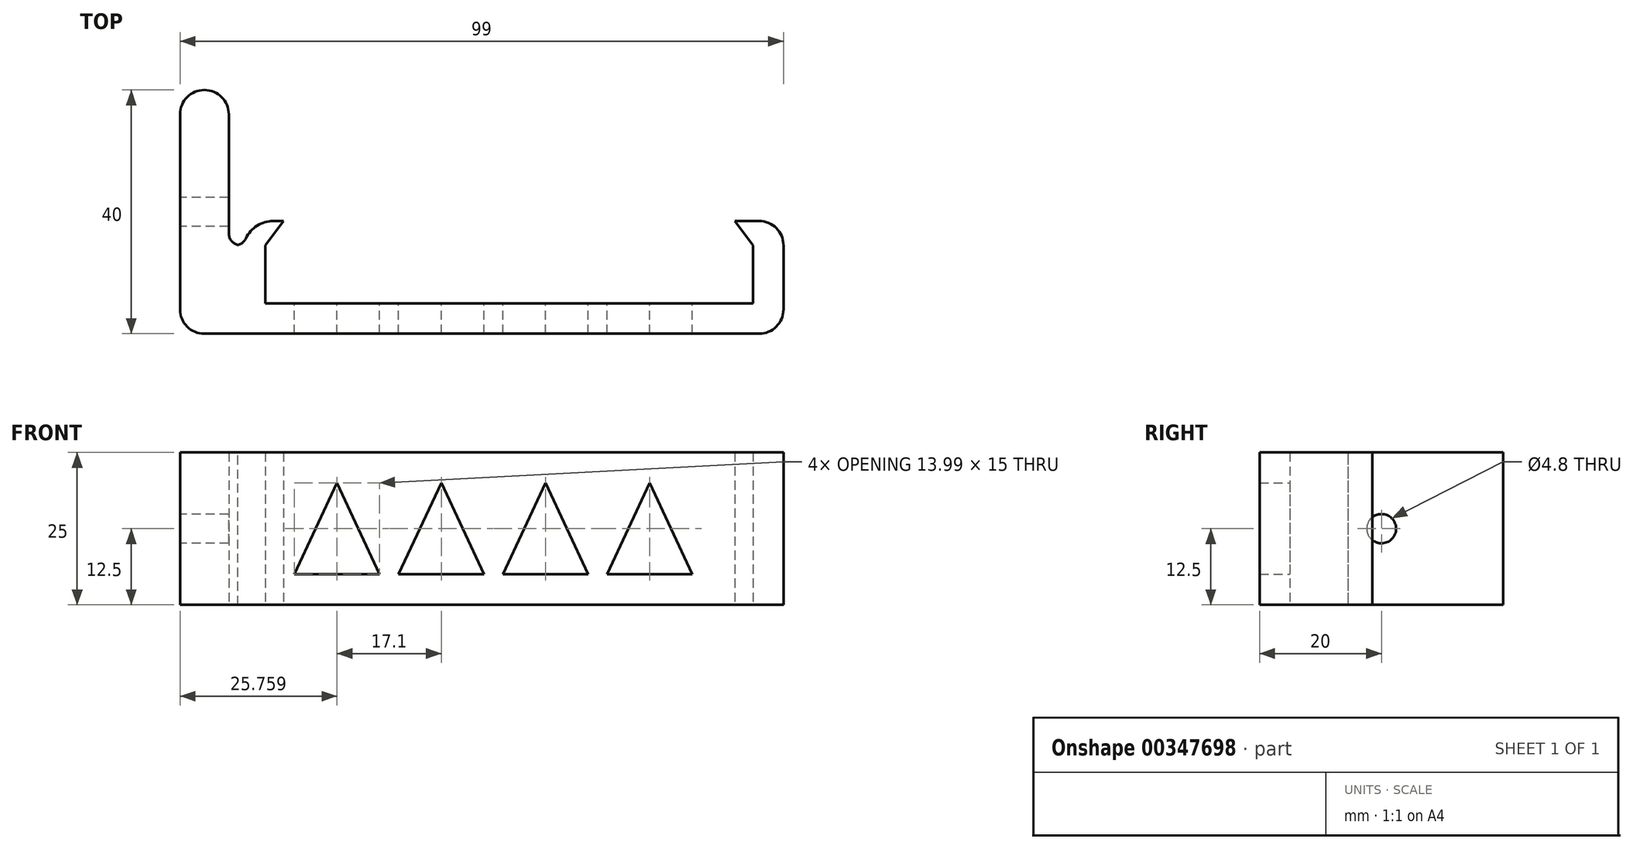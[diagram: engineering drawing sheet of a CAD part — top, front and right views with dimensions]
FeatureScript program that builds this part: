
annotation { "Feature Type Name" : "Feature", "Feature Type Description" : "" }
export const myFeature = defineFeature(function(context is Context, id is Id, definition is map)
    precondition{}
    {
        {
            var Q0;
            Q0=qCreatedBy(makeId("Top.planeOp"),FACE);
            var sketch = newSketch(context, id + "F0", { "sketchPlane" : qUnion([Q0])});
            skLineSegment(sketch, "E0", {"start": v(0, 40) * mm, "end": v(8, 40) * mm});
            skLineSegment(sketch, "E1", {"start": v(8, 40) * mm, "end": v(8, 14.5) * mm});
            skLineSegment(sketch, "E2", {"start": v(8, 14.5) * mm, "end": v(11, 14.5) * mm});
            skLineSegment(sketch, "E3", {"start": v(11, 14.5) * mm, "end": v(11, 18.5) * mm});
            skLineSegment(sketch, "E4", {"start": v(11, 18.5) * mm, "end": v(17, 18.5) * mm});
            skLineSegment(sketch, "E5", {"start": v(17, 18.5) * mm, "end": v(14, 14.5) * mm});
            skLineSegment(sketch, "E6", {"start": v(14, 14.5) * mm, "end": v(14, 5) * mm});
            skLineSegment(sketch, "E7", {"start": v(14, 5) * mm, "end": v(94, 5) * mm});
            skLineSegment(sketch, "E8", {"start": v(94, 5) * mm, "end": v(94, 14.5) * mm});
            skLineSegment(sketch, "E9", {"start": v(99, 18.5) * mm, "end": v(99, 0) * mm});
            skLineSegment(sketch, "E10", {"start": v(99, 0) * mm, "end": v(0, 0) * mm});
            skLineSegment(sketch, "E11", {"start": v(0, 40) * mm, "end": v(0, 0) * mm});
            skLineSegment(sketch, "E12", {"start": v(99, 18.5) * mm, "end": v(91, 18.5) * mm});
            skLineSegment(sketch, "E13", {"start": v(91, 18.5) * mm, "end": v(94, 14.5) * mm});
            skSolve(sketch);
        }
        {
            var Q0;
            Q0 = qSketchRegion(id + "F0", true);
            extrude(context, id + "F1", {"entities" : qUnion([Q0]), "depth" : 25 * mm});
        }
        {
            var Q0;
            Q0=makeQuery(id+"F1.opExtrude","SWEPT_EDGE",EDGE,{"disambiguationData":[OSD([sQuery(id+"F0.wireOp",EDGE,"E2"),sQuery(id+"F0.wireOp",EDGE,"E3")])]});
            var Q1;
            Q1=makeQuery(id+"F1.opExtrude","SWEPT_EDGE",EDGE,{"disambiguationData":[OSD([sQuery(id+"F0.wireOp",EDGE,"E1"),sQuery(id+"F0.wireOp",EDGE,"E2")])]});
            fillet(context, id + "F2", {"entities" : qUnion([Q0, Q1]), "radius" : 2 * mm, "tangentPropagation" : true, "allowEdgeOverflow" : false});
        }
        {
            var Q0;
            Q0=makeQuery(id+"F1.opExtrude","SWEPT_EDGE",EDGE,{"disambiguationData":[OSD([sQuery(id+"F0.wireOp",EDGE,"E3"),sQuery(id+"F0.wireOp",EDGE,"E4")])]});
            fillet(context, id + "F3", {"entities" : qUnion([Q0]), "radius" : 5 * mm, "tangentPropagation" : true, "allowEdgeOverflow" : false});
        }
        {
            var Q0;
            Q0=makeQuery(id+"F1.opExtrude","SWEPT_EDGE",EDGE,{"disambiguationData":[OSD([sQuery(id+"F0.wireOp",EDGE,"E9"),sQuery(id+"F0.wireOp",EDGE,"E12")])]});
            var Q1;
            Q1=makeQuery(id+"F1.opExtrude","SWEPT_EDGE",EDGE,{"disambiguationData":[OSD([sQuery(id+"F0.wireOp",EDGE,"E9"),sQuery(id+"F0.wireOp",EDGE,"E10")])]});
            var Q2;
            Q2=makeQuery(id+"F1.opExtrude","SWEPT_EDGE",EDGE,{"disambiguationData":[OSD([sQuery(id+"F0.wireOp",EDGE,"E10"),sQuery(id+"F0.wireOp",EDGE,"E11")])]});
            var Q3;
            Q3=makeQuery(id+"F1.opExtrude","SWEPT_EDGE",EDGE,{"disambiguationData":[OSD([sQuery(id+"F0.wireOp",EDGE,"E0"),sQuery(id+"F0.wireOp",EDGE,"E11")])]});
            var Q4;
            Q4=makeQuery(id+"F1.opExtrude","SWEPT_EDGE",EDGE,{"disambiguationData":[OSD([sQuery(id+"F0.wireOp",EDGE,"E0"),sQuery(id+"F0.wireOp",EDGE,"E1")])]});
            fillet(context, id + "F4", {"entities" : qUnion([Q0, Q1, Q2, Q3, Q4]), "radius" : 4 * mm, "tangentPropagation" : true, "allowEdgeOverflow" : false});
        }
        {
            var Q0;
            Q0=makeQuery(id+"F1.opExtrude","SWEPT_FACE",FACE,{"disambiguationData":[OSD([sQuery(id+"F0.wireOp",EDGE,"E11")])]});
            var sketch = newSketch(context, id + "F5", { "sketchPlane" : qUnion([Q0])});
            skCircle(sketch, "E14", {"center": v(-20, 12.5) * mm, "radius": 2.4 * mm});
            skPoint(sketch, "E14.centerSnap0", {"position": v(-20, 25) * mm});
            skPoint(sketch, "E14.centerSnap1", {"position": v(-36, 12.5) * mm});
            skSolve(sketch);
        }
        {
            var Q0;
            Q0 = qSketchRegion(id + "F5", true);
            extrude(context, id + "F6", {"entities" : qUnion([Q0]), "operationType" : NewBodyOperationType.REMOVE, "endBound" : BoundingType.UP_TO_NEXT, "oppositeDirection" : true, "depth" : 25 * mm});
        }
        {
            var Q0;
            Q0=makeQuery(id+"F1.opExtrude","SWEPT_FACE",FACE,{"disambiguationData":[OSD([sQuery(id+"F0.wireOp",EDGE,"E7")])]});
            var sketch = newSketch(context, id + "F7", { "sketchPlane" : qUnion([Q0])});
            skLineSegment(sketch, "E15", {"start": v(-84.05, 5) * mm, "end": v(-70.06, 5) * mm});
            skLineSegment(sketch, "E16", {"start": v(-70.06, 5) * mm, "end": v(-77.06, 20) * mm});
            skPoint(sketch, "E16.endSnap0", {"position": v(-77.06, 5) * mm});
            skLineSegment(sketch, "E17", {"start": v(-77.06, 20) * mm, "end": v(-84.05, 5) * mm});
            skPoint(sketch, "E18.1.0.0", {"position": v(-59.96, 5) * mm});
            skLineSegment(sketch, "E18.1.0.1", {"start": v(-52.96, 5) * mm, "end": v(-59.96, 20) * mm});
            skLineSegment(sketch, "E18.1.0.2", {"start": v(-59.96, 20) * mm, "end": v(-66.95, 5) * mm});
            skLineSegment(sketch, "E18.1.0.3", {"start": v(-66.95, 5) * mm, "end": v(-52.96, 5) * mm});
            skPoint(sketch, "E18.2.0.0", {"position": v(-42.86, 5) * mm});
            skLineSegment(sketch, "E18.2.0.1", {"start": v(-35.86, 5) * mm, "end": v(-42.86, 20) * mm});
            skLineSegment(sketch, "E18.2.0.2", {"start": v(-42.86, 20) * mm, "end": v(-49.85, 5) * mm});
            skLineSegment(sketch, "E18.2.0.3", {"start": v(-49.85, 5) * mm, "end": v(-35.86, 5) * mm});
            skPoint(sketch, "E18.3.0.0", {"position": v(-25.76, 5) * mm});
            skLineSegment(sketch, "E18.3.0.1", {"start": v(-18.76, 5) * mm, "end": v(-25.76, 20) * mm});
            skLineSegment(sketch, "E18.3.0.2", {"start": v(-25.76, 20) * mm, "end": v(-32.75, 5) * mm});
            skLineSegment(sketch, "E18.3.0.3", {"start": v(-32.75, 5) * mm, "end": v(-18.76, 5) * mm});
            skLineSegment(sketch, "E18.direction1", {"start": v(-84.05, 5) * mm, "end": v(-66.95, 5) * mm, "construction": true});
            skSolve(sketch);
        }
        {
            var Q0;
            Q0 = qSketchRegion(id + "F7", true);
            extrude(context, id + "F8", {"entities" : qUnion([Q0]), "operationType" : NewBodyOperationType.REMOVE, "endBound" : BoundingType.UP_TO_NEXT, "oppositeDirection" : true, "depth" : 25 * mm});
        }
    });
